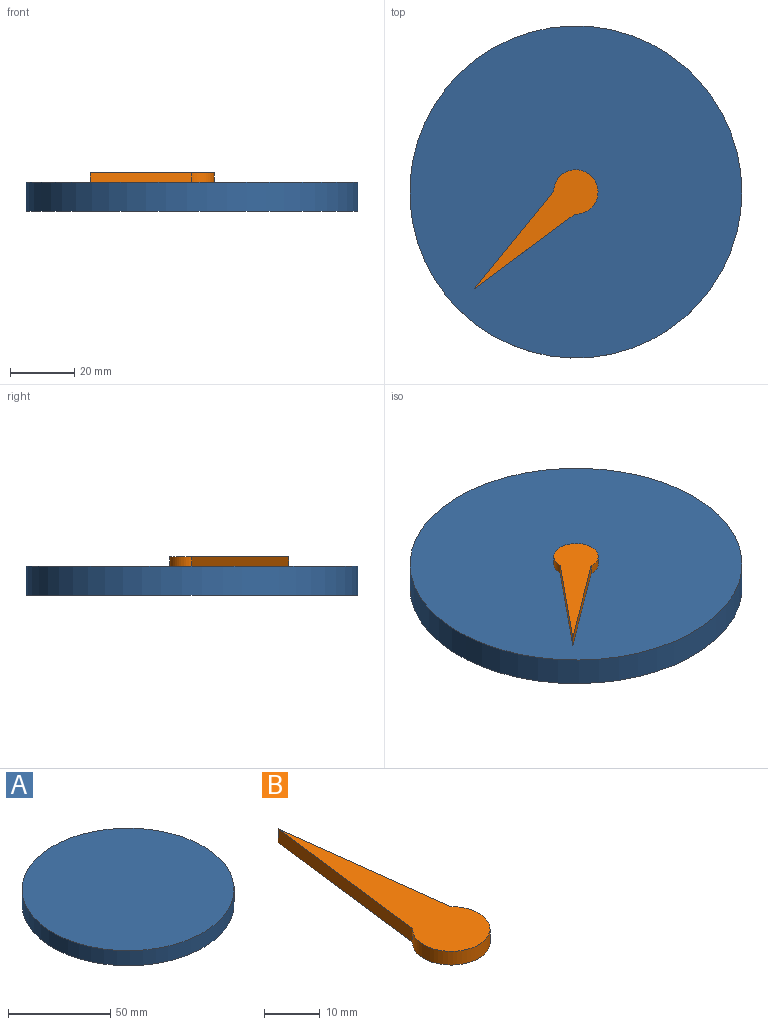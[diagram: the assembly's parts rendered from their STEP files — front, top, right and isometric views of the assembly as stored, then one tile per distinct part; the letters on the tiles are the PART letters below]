
ASSEMBLY  parts=2 mates=1
PART A: 3 faces, bbox 103.7x103.7x9 mm
  f0: cylinder r=51.85mm len=103.7mm, axis (0,0,-1), area 2932.2mm2, adj f1,f2
  f1: plane 103.7x103.7mm, normal (0,0,1), area 8446.7mm2, adj f0
  f2: plane 103.7x103.7mm, normal (0,0,-1), area 8446.7mm2, adj f0
PART B: 5 faces, bbox 13.9x50.7x3 mm
  f0: cylinder r=6.94mm len=13.87mm, axis (0,0,-1), area 98.6mm2, adj f1,f2,f3,f4
  f1: plane 38.84x4.84mm, normal (0.99,0.12,0), area 117.4mm2, adj f0,f2,f3,f4
  f2: plane 38.84x4.84mm, normal (-0.99,0.12,0), area 117.4mm2, adj f0,f1,f3,f4
  f3: plane 50.75x13.87mm, normal (0,0,1), area 325.9mm2, adj f0,f1,f2
  f4: plane 50.75x13.87mm, normal (0,0,-1), area 325.9mm2, adj f0,f1,f2
PLACE A at identity fixed
PLACE B rot(axis=(0,0,1),133.7deg) t=(0,0,0)mm
MATE revolute A.f0 <-> B.f0  axis (0,0,1) through (0,0,9)mm
